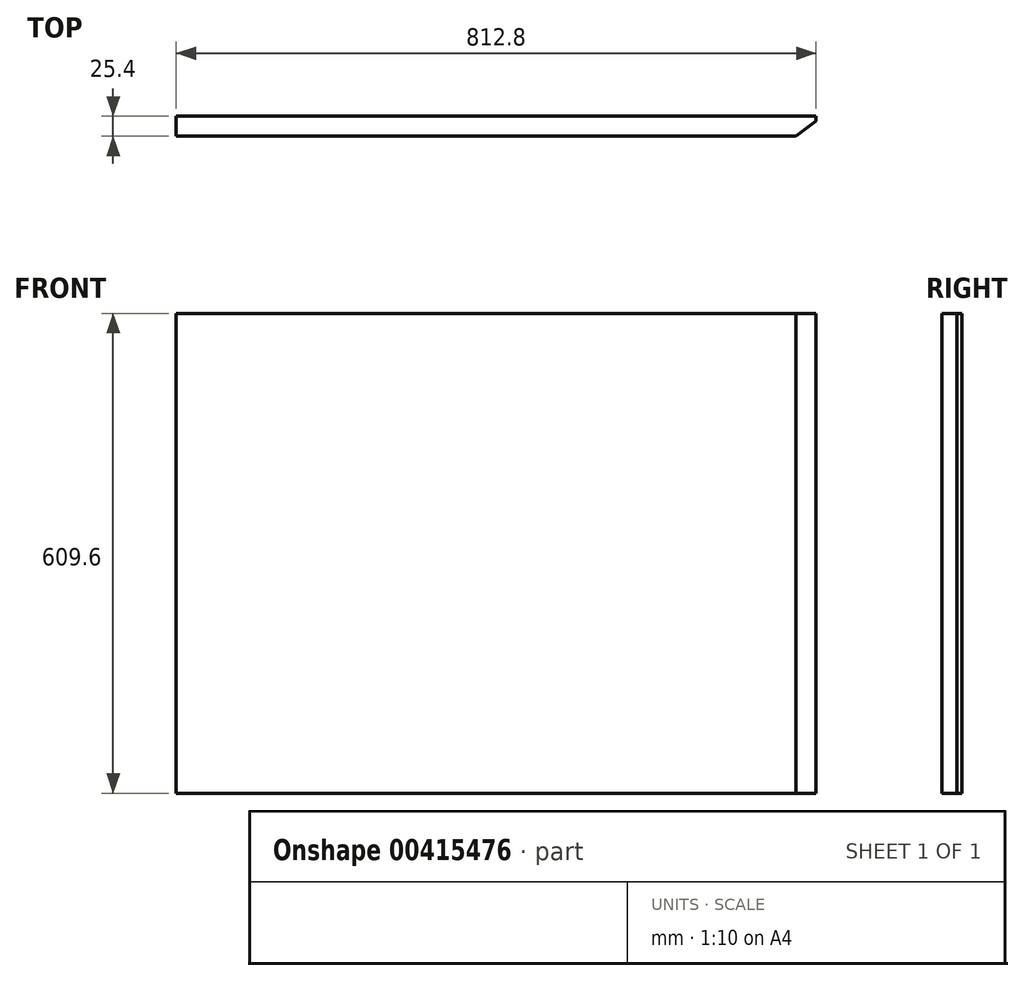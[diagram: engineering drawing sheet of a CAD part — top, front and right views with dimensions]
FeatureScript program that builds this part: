
annotation { "Feature Type Name" : "Feature", "Feature Type Description" : "" }
export const myFeature = defineFeature(function(context is Context, id is Id, definition is map)
    precondition{}
    {
        {
            var Q0;
            Q0=qCreatedBy(makeId("Front.planeOp"),FACE);
            var sketch = newSketch(context, id + "F0", { "sketchPlane" : qUnion([Q0])});
            skLineSegment(sketch, "E0.bottom", {"start": v(406.4, -304.8) * mm, "end": v(-406.4, -304.8) * mm});
            skLineSegment(sketch, "E0.top", {"start": v(406.4, 304.8) * mm, "end": v(-406.4, 304.8) * mm});
            skLineSegment(sketch, "E0.left", {"start": v(406.4, -304.8) * mm, "end": v(406.4, 304.8) * mm});
            skLineSegment(sketch, "E0.right", {"start": v(-406.4, -304.8) * mm, "end": v(-406.4, 304.8) * mm});
            skPoint(sketch, "E0.middle", {"position": v(0, 0) * mm});
            skSolve(sketch);
        }
        {
            var Q0;
            Q0=makeQuery(id+"F0.imprint","IMPRINT",FACE,{"disambiguationData":[TD([[makeQuery(id+"F0.imprint","IMPRINT",EDGE,{"derivedFrom":sQuery(id+"F0.wireOp",EDGE,"E0.bottom")}),-1.0]])]});
            extrude(context, id + "F1", {"entities" : qUnion([Q0]), "depth" : 25.4 * mm});
        }
        {
            var Q0;
            Q0=makeQuery(id+"F1.opExtrude","CAP_EDGE",EDGE,{"disambiguationData":[OSD([sQuery(id+"F0.wireOp",EDGE,"E0.left")])],"isStart":false});
            chamfer(context, id + "F2", {"entities" : qUnion([Q0]), "chamferType" : ChamferType.TWO_OFFSETS, "width1" : 19.05 * mm, "oppositeDirection" : true, "width2" : 25.4 * mm, "tangentPropagation" : true});
        }
    });
